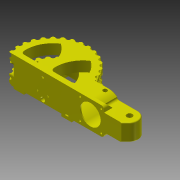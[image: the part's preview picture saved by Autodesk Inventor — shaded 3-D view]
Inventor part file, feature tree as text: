
AUTODESK INVENTOR PART (.ipt)
format: ipt  version: 2013 (Build 170138000, 138)  size: 6,561,280 bytes
history: native  units: mm
features: sketch x34, extrude x33, fillet x7, projected_geometry x6, other x3, chamfer x3, revolve x1
ambient origin geometry x8: Origin, YZ Plane, XZ Plane, XY Plane, X Axis, Y Axis, Z Axis, Center Point
bodies: Solid1 (feature_tree)
feature tree (87):
  other  "_GEARS.iam"
  other  "gear.ipt:1"
  other  "gear.ipt:2"
  extrude  "Extrusion1"  Depth=7.5mm TaperAngle=0.0deg
  extrude  "Extrusion2"  Depth=15.0mm
  extrude  "Extrusion3"  Depth=10.0mm TaperAngle=0.0deg
  extrude  "Extrusion4"  Depth=7.5mm
  extrude  "Extrusion5"  Depth=35.0mm
  extrude  "Extrusion6"  TaperAngle=135.0deg  [1 undecoded]
  extrude  "Extrusion7"  Depth=100.0mm
  extrude  "Extrusion11"  Depth=7.5mm
  extrude  "Extrusion9"  Depth=7.5mm
  extrude  "Extrusion10"  Depth=5.0mm
  extrude  "Extrusion12"  Depth=8.2mm
  extrude  "Extrusion13"  Depth=25.0mm TaperAngle=0.0deg
  extrude  "Extrusion14"  Depth=6.0mm TaperAngle=0.0deg
  extrude  "Extrusion15"  Depth=3.5mm TaperAngle=0.0deg
  extrude  "Extrusion16"  Depth=30.0mm
  fillet  "Fillet1"  Radius=35.0mm
  fillet  "Fillet2"  Radius=10.0mm
  extrude  "Extrusion17"  Depth=80.0mm
  extrude  "Extrusion18"  Depth=10.0mm TaperAngle=0.0deg
  extrude  "Extrusion19"  Depth=6.5mm
  extrude  "Extrusion20"  Depth=10.3mm
  extrude  "Extrusion21"  Depth=7.6333mm
  extrude  "Extrusion22"  Depth=11.0mm TaperAngle=0.0deg
  extrude  "Extrusion23"  Depth=3.0mm
  chamfer  "Chamfer2"  Distance=15.0mm
  fillet  "Fillet3"  Radius=45.0mm
  extrude  "Extrusion24"  Depth=15.0mm TaperAngle=0.0deg
  fillet  "Fillet4"  Radius=3.75mm
  extrude  "Extrusion25"  Depth=42.0mm
  extrude  "Extrusion26"  Depth=5.0mm TaperAngle=0.0deg
  extrude  "Extrusion28"  Depth=70.0mm
  extrude  "Extrusion29"  Depth=3.2mm
  revolve  "Revolution1"  [1 undecoded]
  extrude  "Extrusion30"  Depth=70.0mm
  extrude  "Extrusion31"  Depth=2.5mm TaperAngle=0.0deg
  extrude  "Extrusion32"  Depth=2.5mm TaperAngle=0.0deg
  fillet  "Fillet5"  Radius=35.0mm
  extrude  "Extrusion34"  Depth=2.5mm TaperAngle=0.0deg
  extrude  "Extrusion35"  Depth=89.84mm
  chamfer  "Chamfer3"  Distance=6.35mm
  chamfer  "Chamfer4"  Distance=12.217305mm
  fillet  "Fillet6"  Radius=2.1mm
  fillet  "Fillet7"  Radius=2.5mm
  extrude  "Extrusion36"  Depth=1.0mm TaperAngle=0.0deg
  sketch  "Sketch1"  dims[d0=10.0mm d1=7.5mm d3=0.0mm]
  sketch  "Sketch2"  dims[d2=60.0mm d4=15.0mm]
  sketch  "Sketch3"  dims[d5=125.0mm d6=10.0mm d7=0.0mm]
  sketch  "Sketch4"  dims[d8=48.333333mm d10=7.5mm]
  sketch  "Sketch5"  dims[d11=15.0mm d12=35.0mm]
  sketch  "Sketch6"  dims[d13=27.5mm d14=135.0deg]
  sketch  "Sketch7"  dims[d15=112.5mm d16=100.0mm]
  sketch  "Sketch9"  dims[d17=25.0mm d18=0.0mm d19=7.5mm]
  sketch  "Sketch10"  dims[d21=25.0mm d22=0.0mm d23=7.5mm]
  sketch  "Sketch11"  dims[d24=40.0mm d25=5.0mm]
  sketch  "Sketch12"  dims[d26=25.0mm d27=0.0mm d28=8.2mm]
  sketch  "Sketch13"  dims[d30=35.0mm d31=25.0mm d32=0.0mm]
  sketch  "Sketch14"  dims[d33=13.2mm d34=6.0mm d35=0.0mm]
  sketch  "Sketch15"  dims[d36=7.5mm d38=3.5mm d39=0.0mm]
  sketch  "Sketch16"  dims[d44=10.0mm d45=30.0mm d46=35.0mm d47=10.0mm d48=0.0mm]
  sketch  "Sketch17"  dims[d49=10.0mm d50=0.0mm d54=80.0mm]
  sketch  "Sketch18"  dims[d56=43.75mm d57=10.0mm d58=0.0mm]
  projected_geometry  "Projected Loop1"
  sketch  "Sketch19"  dims[d59=7.64mm d61=6.5mm]
  sketch  "Sketch20"  dims[d62=10.0mm d63=0.0mm d64=10.3mm]
  sketch  "Sketch21"  dims[d66=11.0mm d67=0.0mm d68=7.6333mm]
  sketch  "Sketch22"  dims[d69=2.0mm d70=11.0mm d71=0.0mm]
  projected_geometry  "Projected Loop2"
  sketch  "Sketch23"  dims[d72=12.5mm d73=3.0mm d74=15.0mm d75=0.0mm d76=45.0mm]
  sketch  "Sketch24"  dims[d77=10.0mm d78=15.0mm d79=0.0mm d80=3.75mm]
  projected_geometry  "Projected Loop3"
  projected_geometry  "Projected Loop4"
  projected_geometry  "Projected Loop5"
  sketch  "Sketch25"  dims[d81=3.75mm d82=42.0mm]
  sketch  "Sketch26"  dims[d83=90.0mm d84=5.0mm d85=0.0mm]
  sketch  "Sketch28"  dims[d86=5.0mm d87=0.0mm d88=70.0mm]
  sketch  "Sketch29"  dims[d89=31.0mm d90=3.2mm]
  sketch  "Sketch30"  dims[d91=2.5mm d92=0.0mm d93=30.0mm]
  sketch  "Sketch31"  dims[d95=40.0mm d97=70.0mm]
  sketch  "Sketch32"  dims[d98=2.5mm d99=0.0mm d101=2.5mm d102=0.0mm]
  sketch  "Sketch33"  dims[d103=2.5mm d104=0.0mm d105=2.5mm d106=0.0mm]
  sketch  "Sketch35"  dims[d107=6.0mm d108=2.0mm d109=45.0deg d110=35.0mm]
  projected_geometry  "Projected Loop6"
  sketch  "Sketch36"  dims[d111=6.0mm d113=2.5mm d114=0.0mm]
  sketch  "Sketch37"  dims[d115=4.5mm d116=89.84mm d119=6.35mm d120=12.217305mm d121=2.1mm d122=2.5mm d123=0.0mm d124=1.0mm d125=0.0mm d130=3.0mm d131=0.0mm d132=8.0mm d133=3.0mm d134=0.0mm d135=2.0mm d137=5.0mm d138=4.5mm d139=90.0deg d140=8.2mm d142=3.0mm d143=0.0mm d144=13.2mm d145=6.0mm d146=0.0mm d147=10.0mm d148=0.0mm d149=1.5mm d153=10.0mm d154=0.0mm d155=21.5mm d156=6.0mm d157=10.0mm d158=0.0mm d159=0.5mm d160=3.0mm d161=45.0deg d162=0.5mm d163=3.0mm d164=45.0deg d165=0.5mm d166=0.5mm d167=30.0deg d168=10.0mm d169=0.0mm]
note: 2 required parameter values undecoded (feature->parameter linkage not recoverable at this tier; creation-order binding heuristic only, values carry confidence <= 0.55)